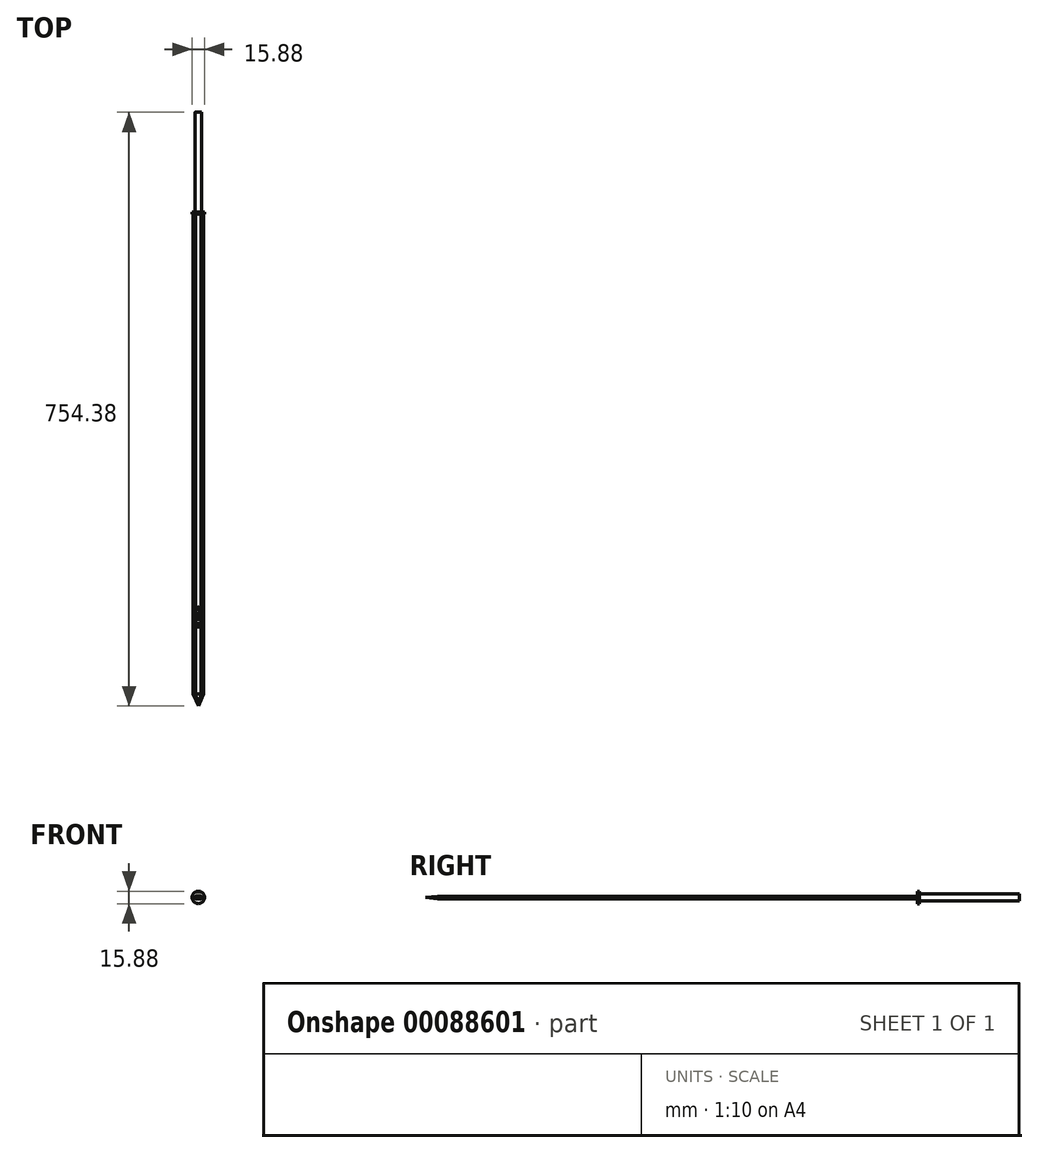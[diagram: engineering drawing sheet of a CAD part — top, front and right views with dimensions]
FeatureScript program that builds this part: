
annotation { "Feature Type Name" : "Feature", "Feature Type Description" : "" }
export const myFeature = defineFeature(function(context is Context, id is Id, definition is map)
    precondition{}
    {
        {
            var Q0;
            Q0=qCreatedBy(makeId("Right.planeOp"),FACE);
            var sketch = newSketch(context, id + "F0", { "sketchPlane" : qUnion([Q0])});
            skLineSegment(sketch, "E0.bottom", {"start": v(0, 0) * mm, "end": v(609.6, 0) * mm});
            skLineSegment(sketch, "E0.top", {"start": v(0, -12.7) * mm, "end": v(609.6, -12.7) * mm});
            skLineSegment(sketch, "E0.left", {"start": v(0, 0) * mm, "end": v(0, -12.7) * mm});
            skLineSegment(sketch, "E0.right", {"start": v(609.6, 0) * mm, "end": v(609.6, -12.7) * mm});
            skSolve(sketch);
        }
        {
            var Q0;
            Q0 = qSketchRegion(id + "F0", true);
            extrude(context, id + "F1", {"entities" : qUnion([Q0]), "depth" : 12.7 * mm});
        }
        {
            var Q0;
            Q0=makeQuery(id+"F1.opExtrude","SWEPT_FACE",FACE,{"disambiguationData":[OSD([sQuery(id+"F0.wireOp",EDGE,"E0.left")])]});
            var sketch = newSketch(context, id + "F2", { "sketchPlane" : qUnion([Q0])});
            skLineSegment(sketch, "E1", {"start": v(0, -6.35) * mm, "end": v(0, 0) * mm});
            skLineSegment(sketch, "E2", {"start": v(0, -3.17) * mm, "end": v(0, -6.35) * mm});
            skLineSegment(sketch, "E3", {"start": v(0, -4.76) * mm, "end": v(0, -6.35) * mm});
            skLineSegment(sketch, "E4", {"start": v(0, -4.76) * mm, "end": v(12.7, -4.76) * mm});
            skLineSegment(sketch, "E5", {"start": v(0, -6.35) * mm, "end": v(0, -12.7) * mm});
            skLineSegment(sketch, "E6", {"start": v(0, -6.35) * mm, "end": v(0, -9.52) * mm});
            skLineSegment(sketch, "E7", {"start": v(0, -6.35) * mm, "end": v(0, -7.94) * mm});
            skLineSegment(sketch, "E8", {"start": v(0, -7.94) * mm, "end": v(12.7, -7.94) * mm});
            skSolve(sketch);
        }
        {
            var Q0;
            Q0 = qSketchRegion(id + "F2", true);
            var Q1;
            Q1=makeQuery(id+"F2.imprint","IMPRINT",FACE,{"disambiguationData":[TD([[makeQuery(id+"F2.imprint","IMPRINT",EDGE,{"derivedFrom":sQuery(id+"F2.wireOp",EDGE,"E1")}),1.0]])]});
            var Q2;
            Q2=makeQuery(id+"F2.imprint","IMPRINT",FACE,{"disambiguationData":[TD([[makeQuery(id+"F2.imprint","IMPRINT",EDGE,{"derivedFrom":sQuery(id+"F2.wireOp",EDGE,"E5")}),1.0]])]});
            extrude(context, id + "F3", {"entities" : qUnion([Q0, Q1, Q2]), "operationType" : NewBodyOperationType.REMOVE, "oppositeDirection" : true, "depth" : 2286 * mm});
        }
        {
            var Q0;
            Q0=makeQuery(id+"F1.opExtrude","SWEPT_FACE",FACE,{"disambiguationData":[OSD([sQuery(id+"F0.wireOp",EDGE,"E0.left")])]});
            var sketch = newSketch(context, id + "F4", { "sketchPlane" : qUnion([Q0])});
            skLineSegment(sketch, "E9", {"start": v(0, -6.35) * mm, "end": v(2.75, -4.76) * mm});
            skLineSegment(sketch, "E10", {"start": v(0, -6.35) * mm, "end": v(2.75, -7.94) * mm});
            skLineSegment(sketch, "E11", {"start": v(12.7, -6.35) * mm, "end": v(9.95, -7.94) * mm});
            skLineSegment(sketch, "E12", {"start": v(12.7, -6.35) * mm, "end": v(9.95, -4.76) * mm});
            skSolve(sketch);
        }
        {
            var Q0;
            Q0 = qSketchRegion(id + "F4", true);
            var Q1;
            {var subQ0=sQuery(id+"F4.wireOp",EDGE,"E9");Q1=makeQuery(id+"F4.imprint","IMPRINT",FACE,{"disambiguationData":[TD([[makeQuery(id+"F4.imprint","IMPRINT",EDGE,{"derivedFrom":subQ0}),1.0]])]});}
            var Q2;
            {var subQ0=sQuery(id+"F4.wireOp",EDGE,"E10");Q2=makeQuery(id+"F4.imprint","IMPRINT",FACE,{"disambiguationData":[TD([[makeQuery(id+"F4.imprint","IMPRINT",EDGE,{"derivedFrom":subQ0}),-1.0]])]});}
            var Q3;
            {var subQ0=sQuery(id+"F4.wireOp",EDGE,"E11");Q3=makeQuery(id+"F4.imprint","IMPRINT",FACE,{"disambiguationData":[TD([[makeQuery(id+"F4.imprint","IMPRINT",EDGE,{"derivedFrom":subQ0}),1.0]])]});}
            var Q4;
            {var subQ0=sQuery(id+"F4.wireOp",EDGE,"E12");Q4=makeQuery(id+"F4.imprint","IMPRINT",FACE,{"disambiguationData":[TD([[makeQuery(id+"F4.imprint","IMPRINT",EDGE,{"derivedFrom":subQ0}),-1.0]])]});}
            extrude(context, id + "F5", {"entities" : qUnion([Q0, Q1, Q2, Q3, Q4]), "operationType" : NewBodyOperationType.REMOVE, "oppositeDirection" : true, "depth" : 2286 * mm});
        }
        {
            var Q0;
            Q0=makeQuery(id+"F1.opExtrude","SWEPT_FACE",FACE,{"disambiguationData":[OSD([sQuery(id+"F0.wireOp",EDGE,"E0.right")])]});
            var sketch = newSketch(context, id + "F6", { "sketchPlane" : qUnion([Q0])});
            skLineSegment(sketch, "E13.bottom", {"start": v(-9.95, -4.76) * mm, "end": v(-2.75, -4.76) * mm});
            skLineSegment(sketch, "E13.top", {"start": v(-9.95, -7.94) * mm, "end": v(-2.75, -7.94) * mm});
            skLineSegment(sketch, "E13.left", {"start": v(-9.95, -4.76) * mm, "end": v(-9.95, -7.94) * mm});
            skLineSegment(sketch, "E13.right", {"start": v(-2.75, -4.76) * mm, "end": v(-2.75, -7.94) * mm});
            skLineSegment(sketch, "E14", {"start": v(-9.95, -6.35) * mm, "end": v(-22.65, -6.35) * mm});
            skLineSegment(sketch, "E15", {"start": v(-2.75, -6.35) * mm, "end": v(9.95, -6.35) * mm});
            skLineSegment(sketch, "E16", {"start": v(-6.35, -4.76) * mm, "end": v(-6.35, 1.59) * mm});
            skLineSegment(sketch, "E17", {"start": v(-6.35, -7.94) * mm, "end": v(-6.35, -14.29) * mm});
            skLineSegment(sketch, "E18", {"start": v(-22.65, -6.35) * mm, "end": v(-6.35, 1.59) * mm});
            skLineSegment(sketch, "E19", {"start": v(9.95, -6.35) * mm, "end": v(-6.35, 1.59) * mm});
            skLineSegment(sketch, "E20", {"start": v(-22.65, -6.35) * mm, "end": v(-6.35, -14.29) * mm});
            skLineSegment(sketch, "E21", {"start": v(9.95, -6.35) * mm, "end": v(-6.35, -14.29) * mm});
            skLineSegment(sketch, "E22", {"start": v(-6.35, -4.76) * mm, "end": v(-6.35, -7.94) * mm});
            skCircle(sketch, "E23", {"center": v(-6.35, -6.35) * mm, "radius": 7.94 * mm});
            skSolve(sketch);
        }
        {
            var Q0;
            {var subQ2=sQuery(id+"F6.wireOp",EDGE,"E16");Q0=makeQuery(id+"F6.imprint","IMPRINT",FACE,{"disambiguationData":[TD([[makeQuery(id+"F6.imprint","IMPRINT",EDGE,{"derivedFrom":subQ2}),1.0]])]});}
            var Q1;
            {var subQ0=sQuery(id+"F6.wireOp",EDGE,"E23");var subQ1=sQuery(id+"F6.wireOp",EDGE,"E18");var subQ3=makeQuery(id+"F6.imprint","INTERSECT",VERTEX,{"derivedFrom":[subQ1,subQ0]});Q1=makeQuery(id+"F6.imprint","IMPRINT",FACE,{"disambiguationData":[TD([[makeQuery(id+"F6.imprint","IMPRINT",EDGE,{"disambiguationData":[TD([[subQ3,-1.0]])],"derivedFrom":subQ1}),1.0]])]});}
            var Q2;
            {var subQ0=sQuery(id+"F6.wireOp",EDGE,"E23");var subQ1=sQuery(id+"F6.wireOp",EDGE,"E19");var subQ3=makeQuery(id+"F6.imprint","INTERSECT",VERTEX,{"derivedFrom":[subQ1,subQ0]});Q2=makeQuery(id+"F6.imprint","IMPRINT",FACE,{"disambiguationData":[TD([[makeQuery(id+"F6.imprint","IMPRINT",EDGE,{"disambiguationData":[TD([[subQ3,-1.0]])],"derivedFrom":subQ1}),-1.0]])]});}
            var Q3;
            {var subQ0=sQuery(id+"F6.wireOp",EDGE,"E16");Q3=makeQuery(id+"F6.imprint","IMPRINT",FACE,{"disambiguationData":[TD([[makeQuery(id+"F6.imprint","IMPRINT",EDGE,{"derivedFrom":subQ0}),-1.0]])]});}
            var Q4;
            {var subQ2=sQuery(id+"F6.wireOp",EDGE,"E17");Q4=makeQuery(id+"F6.imprint","IMPRINT",FACE,{"disambiguationData":[TD([[makeQuery(id+"F6.imprint","IMPRINT",EDGE,{"derivedFrom":subQ2}),1.0]])]});}
            var Q5;
            {var subQ7=sQuery(id+"F6.wireOp",EDGE,"E22");Q5=makeQuery(id+"F6.imprint","IMPRINT",FACE,{"disambiguationData":[TD([[makeQuery(id+"F6.imprint","IMPRINT",EDGE,{"derivedFrom":subQ7}),1.0]])]});}
            var Q6;
            {var subQ1=makeQuery(id+"F1.opExtrude","SWEPT_FACE",FACE,{"disambiguationData":[OSD([sQuery(id+"F0.wireOp",EDGE,"E0.right")])]});var subQ2=makeQuery(id+"F5.boolean.opBoolean","INTERSECT",EDGE,{"derivedFrom":[subQ1,makeQuery(id+"F5.opExtrude","SWEPT_FACE",FACE,{"disambiguationData":[OSD([sQuery(id+"F4.wireOp",EDGE,"E9")])]})]});Q6=makeQuery(id+"F6.imprint","IMPRINT",FACE,{"disambiguationData":[TD([[makeQuery(id+"F6.imprint","IMPRINT",EDGE,{"derivedFrom":subQ2}),-1.0]])]});}
            var Q7;
            {var subQ1=makeQuery(id+"F1.opExtrude","SWEPT_FACE",FACE,{"disambiguationData":[OSD([sQuery(id+"F0.wireOp",EDGE,"E0.right")])]});var subQ2=makeQuery(id+"F5.boolean.opBoolean","INTERSECT",EDGE,{"derivedFrom":[subQ1,makeQuery(id+"F5.opExtrude","SWEPT_FACE",FACE,{"disambiguationData":[OSD([sQuery(id+"F4.wireOp",EDGE,"E10")])]})]});Q7=makeQuery(id+"F6.imprint","IMPRINT",FACE,{"disambiguationData":[TD([[makeQuery(id+"F6.imprint","IMPRINT",EDGE,{"derivedFrom":subQ2}),1.0]])]});}
            var Q8;
            {var subQ1=makeQuery(id+"F1.opExtrude","SWEPT_FACE",FACE,{"disambiguationData":[OSD([sQuery(id+"F0.wireOp",EDGE,"E0.right")])]});var subQ2=makeQuery(id+"F5.boolean.opBoolean","INTERSECT",EDGE,{"derivedFrom":[subQ1,makeQuery(id+"F5.opExtrude","SWEPT_FACE",FACE,{"disambiguationData":[OSD([sQuery(id+"F4.wireOp",EDGE,"E11")])]})]});Q8=makeQuery(id+"F6.imprint","IMPRINT",FACE,{"disambiguationData":[TD([[makeQuery(id+"F6.imprint","IMPRINT",EDGE,{"derivedFrom":subQ2}),-1.0]])]});}
            var Q9;
            {var subQ1=makeQuery(id+"F1.opExtrude","SWEPT_FACE",FACE,{"disambiguationData":[OSD([sQuery(id+"F0.wireOp",EDGE,"E0.right")])]});var subQ2=makeQuery(id+"F5.boolean.opBoolean","INTERSECT",EDGE,{"derivedFrom":[subQ1,makeQuery(id+"F5.opExtrude","SWEPT_FACE",FACE,{"disambiguationData":[OSD([sQuery(id+"F4.wireOp",EDGE,"E12")])]})]});Q9=makeQuery(id+"F6.imprint","IMPRINT",FACE,{"disambiguationData":[TD([[makeQuery(id+"F6.imprint","IMPRINT",EDGE,{"derivedFrom":subQ2}),1.0]])]});}
            var Q10;
            {var subQ2=sQuery(id+"F6.wireOp",EDGE,"E17");Q10=makeQuery(id+"F6.imprint","IMPRINT",FACE,{"disambiguationData":[TD([[makeQuery(id+"F6.imprint","IMPRINT",EDGE,{"derivedFrom":subQ2}),-1.0]])]});}
            var Q11;
            {var subQ0=sQuery(id+"F6.wireOp",EDGE,"E23");var subQ1=sQuery(id+"F6.wireOp",EDGE,"E20");var subQ3=makeQuery(id+"F6.imprint","INTERSECT",VERTEX,{"derivedFrom":[subQ1,subQ0]});Q11=makeQuery(id+"F6.imprint","IMPRINT",FACE,{"disambiguationData":[TD([[makeQuery(id+"F6.imprint","IMPRINT",EDGE,{"disambiguationData":[TD([[subQ3,-1.0]])],"derivedFrom":subQ1}),-1.0]])]});}
            var Q12;
            {var subQ0=sQuery(id+"F6.wireOp",EDGE,"E23");var subQ1=sQuery(id+"F6.wireOp",EDGE,"E21");var subQ3=makeQuery(id+"F6.imprint","INTERSECT",VERTEX,{"derivedFrom":[subQ1,subQ0]});Q12=makeQuery(id+"F6.imprint","IMPRINT",FACE,{"disambiguationData":[TD([[makeQuery(id+"F6.imprint","IMPRINT",EDGE,{"disambiguationData":[TD([[subQ3,-1.0]])],"derivedFrom":subQ1}),1.0]])]});}
            var Q13;
            {var subQ7=sQuery(id+"F6.wireOp",EDGE,"E22");Q13=makeQuery(id+"F6.imprint","IMPRINT",FACE,{"disambiguationData":[TD([[makeQuery(id+"F6.imprint","IMPRINT",EDGE,{"derivedFrom":subQ7}),-1.0]])]});}
            extrude(context, id + "F7", {"entities" : qUnion([Q0, Q1, Q2, Q3, Q4, Q5, Q6, Q7, Q8, Q9, Q10, Q11, Q12, Q13]), "operationType" : NewBodyOperationType.ADD, "depth" : 2.54 * mm});
        }
        {
            var Q0;
            Q0=makeQuery(id+"F7.opExtrude","CAP_FACE",FACE,{"disambiguationData":[OSD([sQuery(id+"F6.wireOp",EDGE,"E23")])],"isStart":false});
            var sketch = newSketch(context, id + "F8", { "sketchPlane" : qUnion([Q0])});
            skCircle(sketch, "E24", {"center": v(-6.35, -6.35) * mm, "radius": 4.45 * mm});
            skSolve(sketch);
        }
        {
            var Q0;
            Q0 = qSketchRegion(id + "F8", true);
            extrude(context, id + "F9", {"entities" : qUnion([Q0]), "operationType" : NewBodyOperationType.ADD, "depth" : 127 * mm});
        }
        {
            var Q0;
            Q0=makeQuery(id+"F1.opExtrude","SWEPT_FACE",FACE,{"disambiguationData":[OSD([sQuery(id+"F0.wireOp",EDGE,"E0.left")])]});
            cPlane(context, id + "F10", {"entities" : qUnion([Q0]), "cplaneType" : CPlaneType.OFFSET, "offset" : 15.24 * mm, "width" : 152.4 * mm, "height" : 152.4 * mm});
        }
        {
            var Q0;
            Q0=qCreatedBy(id+"F10.planeOp",FACE);
            var sketch = newSketch(context, id + "F11", { "sketchPlane" : qUnion([Q0])});
            skPoint(sketch, "E25", {"position": v(6.47, -6.5) * mm});
            skSolve(sketch);
        }
        {
            var Q1;
            Q1=sQuery(id+"F11.wireOp",VERTEX,"E25");
            var Q2;
            Q2=makeQuery(id+"F1.opExtrude","SWEPT_FACE",FACE,{"disambiguationData":[OSD([sQuery(id+"F0.wireOp",EDGE,"E0.left")])]});
            loft(context, id + "F12", {"operationType" : NewBodyOperationType.ADD, "sheetProfilesArray" : [{ "sheetProfileEntities" : qUnion([Q1]) }, { "sheetProfileEntities" : qUnion([Q2]) }]});
        }
        {
            var Q0;
            Q0=makeQuery(id+"F3.boolean.opBoolean","COPY",FACE,{"derivedFrom":makeQuery(id+"F3.opExtrude","SWEPT_FACE",FACE,{"disambiguationData":[OSD([sQuery(id+"F2.wireOp",EDGE,"E4")])]})});
            var sketch = newSketch(context, id + "F13", { "sketchPlane" : qUnion([Q0])});
            skText(sketch, "E26", { "text": "M\n", "fontName": "OpenSans-Regular.ttf"});
            skText(sketch, "E27", { "text": "G", "fontName": "OpenSans-Regular.ttf"});
            skText(sketch, "E28", { "text": "H\n", "fontName": "OpenSans-Regular.ttf"});
            const initialGuessF13  = {"E26": [0.0024, 0.10564, 1, 0, 0.00636], "E27": [0.00234, 0.09502, 1, 0, 0.00792], "E28": [0.00216, 0.08373, 1, 0, 0.0081]};
            skSetInitialGuess(sketch, initialGuessF13);
            skSolve(sketch);
        }
        {
            var Q0;
            Q0 = qSketchRegion(id + "F13", true);
            extrude(context, id + "F14", {"entities" : qUnion([Q0]), "operationType" : NewBodyOperationType.REMOVE, "oppositeDirection" : true, "depth" : 0.03 * mm});
        }
        {
            var Q0;
            Q0=makeQuery(id+"F14.boolean.opBoolean","COPY",FACE,{"derivedFrom":makeQuery(id+"F14.opExtrude","CAP_FACE",FACE,{"disambiguationData":[OSD([sQuery(id+"F13.wireOp",EDGE,"E28.sketch_text.stroke-0"),sQuery(id+"F13.wireOp",EDGE,"E28.sketch_text.stroke-1"),sQuery(id+"F13.wireOp",EDGE,"E28.sketch_text.stroke-2"),sQuery(id+"F13.wireOp",EDGE,"E28.sketch_text.stroke-3"),sQuery(id+"F13.wireOp",EDGE,"E28.sketch_text.stroke-4"),sQuery(id+"F13.wireOp",EDGE,"E28.sketch_text.stroke-5"),sQuery(id+"F13.wireOp",EDGE,"E28.sketch_text.stroke-6"),sQuery(id+"F13.wireOp",EDGE,"E28.sketch_text.stroke-7"),sQuery(id+"F13.wireOp",EDGE,"E28.sketch_text.stroke-8"),sQuery(id+"F13.wireOp",EDGE,"E28.sketch_text.stroke-9"),sQuery(id+"F13.wireOp",EDGE,"E28.sketch_text.stroke-10"),sQuery(id+"F13.wireOp",EDGE,"E28.sketch_text.stroke-11")])],"isStart":false})});
            var Q1;
            Q1=makeQuery(id+"F14.boolean.opBoolean","COPY",FACE,{"derivedFrom":makeQuery(id+"F14.opExtrude","CAP_FACE",FACE,{"disambiguationData":[OSD([sQuery(id+"F13.wireOp",EDGE,"E27.sketch_text.stroke-0"),sQuery(id+"F13.wireOp",EDGE,"E27.sketch_text.stroke-1"),sQuery(id+"F13.wireOp",EDGE,"E27.sketch_text.stroke-2"),sQuery(id+"F13.wireOp",EDGE,"E27.sketch_text.stroke-3"),sQuery(id+"F13.wireOp",EDGE,"E27.sketch_text.stroke-4"),sQuery(id+"F13.wireOp",EDGE,"E27.sketch_text.stroke-5"),sQuery(id+"F13.wireOp",EDGE,"E27.sketch_text.stroke-6"),sQuery(id+"F13.wireOp",EDGE,"E27.sketch_text.stroke-7"),sQuery(id+"F13.wireOp",EDGE,"E27.sketch_text.stroke-8"),sQuery(id+"F13.wireOp",EDGE,"E27.sketch_text.stroke-9"),sQuery(id+"F13.wireOp",EDGE,"E27.sketch_text.stroke-10"),sQuery(id+"F13.wireOp",EDGE,"E27.sketch_text.stroke-11"),sQuery(id+"F13.wireOp",EDGE,"E27.sketch_text.stroke-12"),sQuery(id+"F13.wireOp",EDGE,"E27.sketch_text.stroke-13"),sQuery(id+"F13.wireOp",EDGE,"E27.sketch_text.stroke-14"),sQuery(id+"F13.wireOp",EDGE,"E27.sketch_text.stroke-15"),sQuery(id+"F13.wireOp",EDGE,"E27.sketch_text.stroke-16"),sQuery(id+"F13.wireOp",EDGE,"E27.sketch_text.stroke-17"),sQuery(id+"F13.wireOp",EDGE,"E27.sketch_text.stroke-18"),sQuery(id+"F13.wireOp",EDGE,"E27.sketch_text.stroke-19")])],"isStart":false})});
            var Q2;
            Q2=makeQuery(id+"F14.boolean.opBoolean","COPY",FACE,{"derivedFrom":makeQuery(id+"F14.opExtrude","CAP_FACE",FACE,{"disambiguationData":[OSD([sQuery(id+"F13.wireOp",EDGE,"E26.sketch_text.stroke-0"),sQuery(id+"F13.wireOp",EDGE,"E26.sketch_text.stroke-1"),sQuery(id+"F13.wireOp",EDGE,"E26.sketch_text.stroke-2"),sQuery(id+"F13.wireOp",EDGE,"E26.sketch_text.stroke-3"),sQuery(id+"F13.wireOp",EDGE,"E26.sketch_text.stroke-4"),sQuery(id+"F13.wireOp",EDGE,"E26.sketch_text.stroke-5"),sQuery(id+"F13.wireOp",EDGE,"E26.sketch_text.stroke-6"),sQuery(id+"F13.wireOp",EDGE,"E26.sketch_text.stroke-7"),sQuery(id+"F13.wireOp",EDGE,"E26.sketch_text.stroke-8"),sQuery(id+"F13.wireOp",EDGE,"E26.sketch_text.stroke-9"),sQuery(id+"F13.wireOp",EDGE,"E26.sketch_text.stroke-10"),sQuery(id+"F13.wireOp",EDGE,"E26.sketch_text.stroke-11"),sQuery(id+"F13.wireOp",EDGE,"E26.sketch_text.stroke-12"),sQuery(id+"F13.wireOp",EDGE,"E26.sketch_text.stroke-13"),sQuery(id+"F13.wireOp",EDGE,"E26.sketch_text.stroke-14"),sQuery(id+"F13.wireOp",EDGE,"E26.sketch_text.stroke-15"),sQuery(id+"F13.wireOp",EDGE,"E26.sketch_text.stroke-16"),sQuery(id+"F13.wireOp",EDGE,"E26.sketch_text.stroke-17")])],"isStart":false})});
            extrude(context, id + "F15", {"entities" : qUnion([Q0, Q1, Q2]), "depth" : 0.01 * mm});
        }
    });
